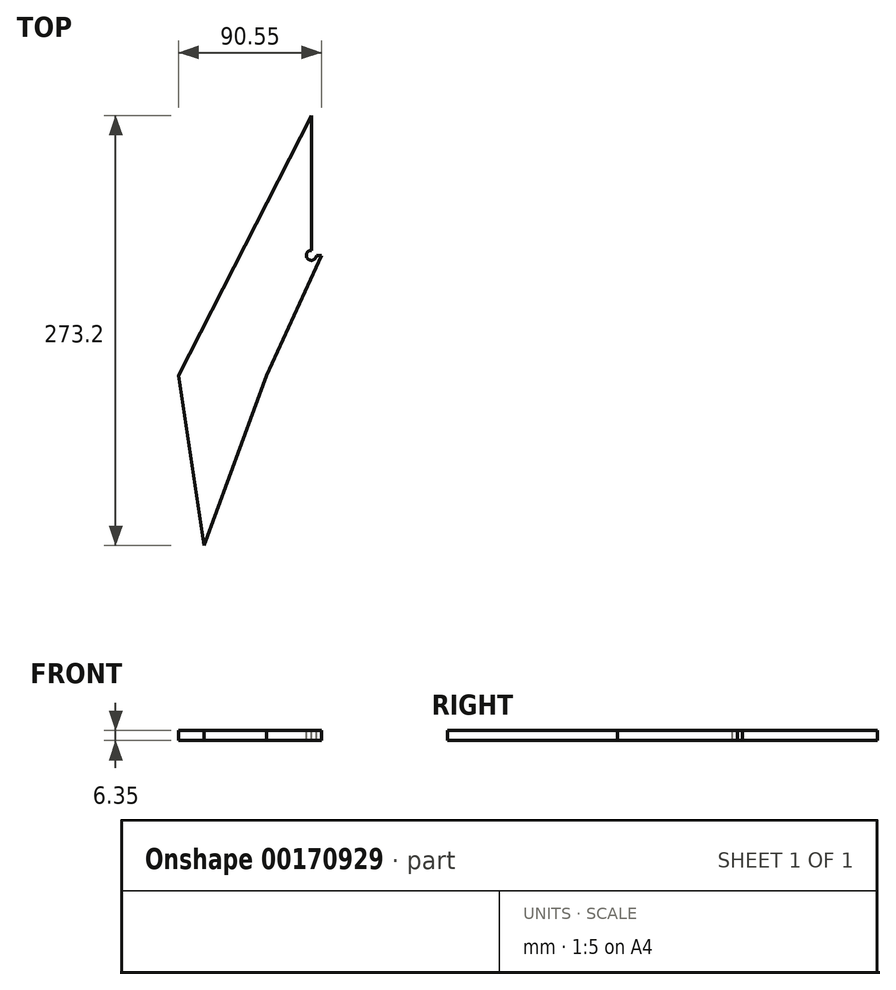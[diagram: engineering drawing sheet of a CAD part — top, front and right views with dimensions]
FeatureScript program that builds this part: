
annotation { "Feature Type Name" : "Feature", "Feature Type Description" : "" }
export const myFeature = defineFeature(function(context is Context, id is Id, definition is map)
    precondition{}
    {
        {
            var Q0;
            Q0=qCreatedBy(makeId("Top.planeOp"),FACE);
            var sketch = newSketch(context, id + "F0", { "sketchPlane" : qUnion([Q0])});
            skLineSegment(sketch, "E0.bottom", {"start": v(-304.8, 180.98) * mm, "end": v(-27.05, 180.98) * mm});
            skLineSegment(sketch, "E0.top", {"start": v(-304.8, 0) * mm, "end": v(0, 0) * mm});
            skLineSegment(sketch, "E0.left", {"start": v(-304.8, 180.98) * mm, "end": v(-304.8, 0) * mm});
            skLineSegment(sketch, "E1", {"start": v(-278.2, 257.18) * mm, "end": v(284.57, 257.18) * mm, "construction": true});
            skLineSegment(sketch, "E2", {"start": v(57.15, 445.1) * mm, "end": v(57.15, 257.18) * mm, "construction": true});
            skLineSegment(sketch, "E3", {"start": v(0, 0) * mm, "end": v(-27.05, 180.98) * mm});
            skLineSegment(sketch, "E4.bottom", {"start": v(57.15, 257.18) * mm, "end": v(63.5, 257.18) * mm});
            skLineSegment(sketch, "E4.top", {"start": v(57.15, 377.83) * mm, "end": v(63.5, 377.83) * mm});
            skLineSegment(sketch, "E4.left", {"start": v(57.15, 257.18) * mm, "end": v(57.15, 377.83) * mm});
            skLineSegment(sketch, "E4.right", {"start": v(63.5, 257.18) * mm, "end": v(63.5, 377.83) * mm});
            skPoint(sketch, "E5", {"position": v(-77.85, 180.98) * mm});
            skPoint(sketch, "E6", {"position": v(57.15, 320.68) * mm});
            skLineSegment(sketch, "E7", {"start": v(57.15, 320.68) * mm, "end": v(-77.85, 180.98) * mm, "construction": true});
            skPoint(sketch, "E8", {"position": v(57.15, 346.08) * mm});
            skLineSegment(sketch, "E9", {"start": v(57.15, 346.08) * mm, "end": v(-27.05, 180.97) * mm});
            skLineSegment(sketch, "E10.trimOffspring", {"start": v(57.15, 123.28) * mm, "end": v(57.15, -128.15) * mm, "construction": true});
            skLineSegment(sketch, "E11", {"start": v(196.73, 196.85) * mm, "end": v(-77.42, 196.85) * mm, "construction": true});
            skLineSegment(sketch, "E12", {"start": v(197.16, 180.98) * mm, "end": v(-52.54, 180.98) * mm, "construction": true});
            skLineSegment(sketch, "E13", {"start": v(28.57, 311.63) * mm, "end": v(28.58, 51.2) * mm, "construction": true});
            skLineSegment(sketch, "E14", {"start": v(0, 0) * mm, "end": v(28.58, 180.98) * mm});
            skLineSegment(sketch, "E15", {"start": v(28.58, 180.98) * mm, "end": v(56.96, 180.98) * mm});
            skLineSegment(sketch, "E16", {"start": v(56.96, 180.98) * mm, "end": v(56.96, 196.85) * mm});
            skLineSegment(sketch, "E17", {"start": v(56.96, 196.85) * mm, "end": v(196.73, 196.85) * mm});
            skLineSegment(sketch, "E18", {"start": v(121.86, 333.18) * mm, "end": v(-70.44, -43.9) * mm, "construction": true});
            skLineSegment(sketch, "E19", {"start": v(-10.9, 72.88) * mm, "end": v(28.58, 180.98) * mm});
            skLineSegment(sketch, "E20", {"start": v(28.57, 180.98) * mm, "end": v(63.5, 257.18) * mm});
            skSolve(sketch);
        }
        {
            var Q0;
            {var subQ2=sQuery(id+"F0.wireOp",EDGE,"E4.bottom");Q0=makeQuery(id+"F0.imprint","IMPRINT",FACE,{"disambiguationData":[TD([[makeQuery(id+"F0.imprint","IMPRINT",EDGE,{"derivedFrom":subQ2}),-1.0]])]});}
            extrude(context, id + "F1", {"entities" : qUnion([Q0]), "depth" : 6.35 * mm});
        }
        {
            var Q0;
            Q0=makeQuery(id+"F1.opExtrude","CAP_FACE",FACE,{"disambiguationData":[OSD([sQuery(id+"F0.wireOp",EDGE,"E3"),sQuery(id+"F0.wireOp",EDGE,"E4.bottom"),sQuery(id+"F0.wireOp",EDGE,"E4.left"),sQuery(id+"F0.wireOp",EDGE,"E9"),sQuery(id+"F0.wireOp",EDGE,"Les2eWQ0-JGy5-8q6Y-nYQp-P82S8m8KlBT8"),sQuery(id+"F0.wireOp",EDGE,"kmL3bMQX-UUCI-flXM-k52j-fnWwU542hpqI")])],"isStart":false});
            var sketch = newSketch(context, id + "F2", { "sketchPlane" : qUnion([Q0])});
            skCircle(sketch, "E21", {"center": v(57.15, 257.18) * mm, "radius": 3.18 * mm});
            skSolve(sketch);
        }
        {
            var Q0;
            {var subQ0=sQuery(id+"F2.wireOp",EDGE,"E21");var subQ1=makeQuery(id+"F1.opExtrude","CAP_EDGE",EDGE,{"disambiguationData":[OSD([sQuery(id+"F0.wireOp",EDGE,"E4.bottom")])],"isStart":false});var subQ2=makeQuery(id+"F2.imprint","INTERSECT",VERTEX,{"derivedFrom":[subQ1,subQ0]});Q0=makeQuery(id+"F2.imprint","IMPRINT",FACE,{"disambiguationData":[TD([[makeQuery(id+"F2.imprint","IMPRINT",EDGE,{"disambiguationData":[TD([[subQ2,1.0]])],"derivedFrom":subQ0}),1.0]])]});}
            extrude(context, id + "F3", {"entities" : qUnion([Q0]), "operationType" : NewBodyOperationType.REMOVE, "oppositeDirection" : true, "depth" : 25.4 * mm});
        }
    });
